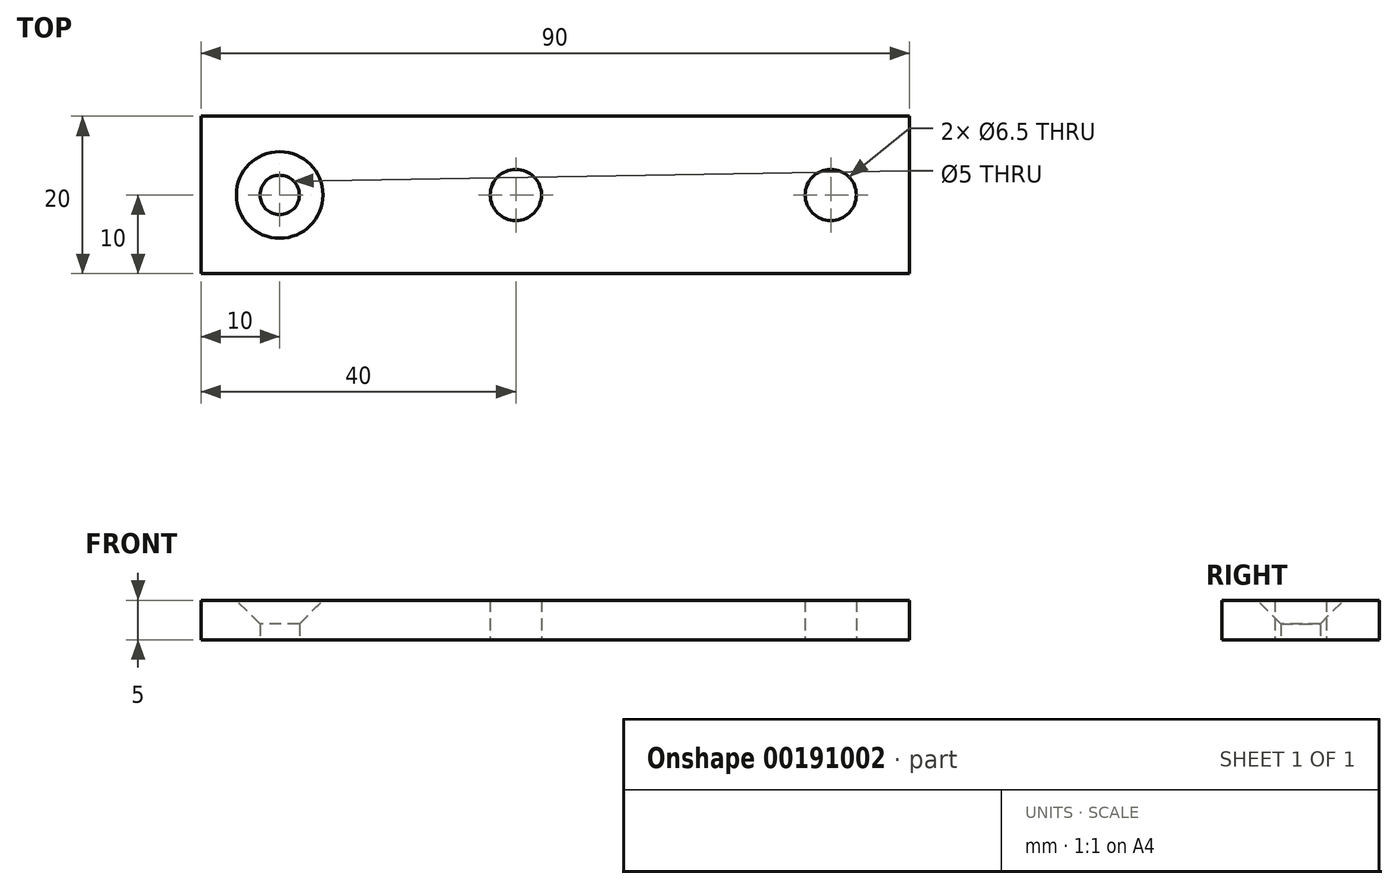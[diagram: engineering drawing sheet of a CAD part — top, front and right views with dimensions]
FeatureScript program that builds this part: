
annotation { "Feature Type Name" : "Feature", "Feature Type Description" : "" }
export const myFeature = defineFeature(function(context is Context, id is Id, definition is map)
    precondition{}
    {
        {
            var Q0;
            Q0=qCreatedBy(makeId("Top.planeOp"),FACE);
            var sketch = newSketch(context, id + "F0", { "sketchPlane" : qUnion([Q0])});
            skLineSegment(sketch, "E0.bottom", {"start": v(-10, 10) * mm, "end": v(80, 10) * mm});
            skLineSegment(sketch, "E0.top", {"start": v(-10, -10) * mm, "end": v(80, -10) * mm});
            skLineSegment(sketch, "E0.left", {"start": v(-10, 10) * mm, "end": v(-10, -10) * mm});
            skLineSegment(sketch, "E0.right", {"start": v(80, 10) * mm, "end": v(80, -10) * mm});
            skCircle(sketch, "E1", {"center": v(0, 0) * mm, "radius": 2.5 * mm});
            skCircle(sketch, "E2", {"center": v(30, 0) * mm, "radius": 3.25 * mm});
            skCircle(sketch, "E3", {"center": v(70, 0) * mm, "radius": 3.25 * mm});
            skSolve(sketch);
        }
        {
            var Q0;
            Q0 = qSketchRegion(id + "F0", true);
            extrude(context, id + "F1", {"entities" : qUnion([Q0]), "depth" : 5 * mm});
        }
        {
            var Q0;
            Q0=makeQuery(id+"F1.opExtrude","CAP_EDGE",EDGE,{"disambiguationData":[OSD([sQuery(id+"F0.wireOp",EDGE,"E1")])],"isStart":false});
            chamfer(context, id + "F2", {"entities" : qUnion([Q0]), "width" : 3 * mm, "tangentPropagation" : true});
        }
    });
